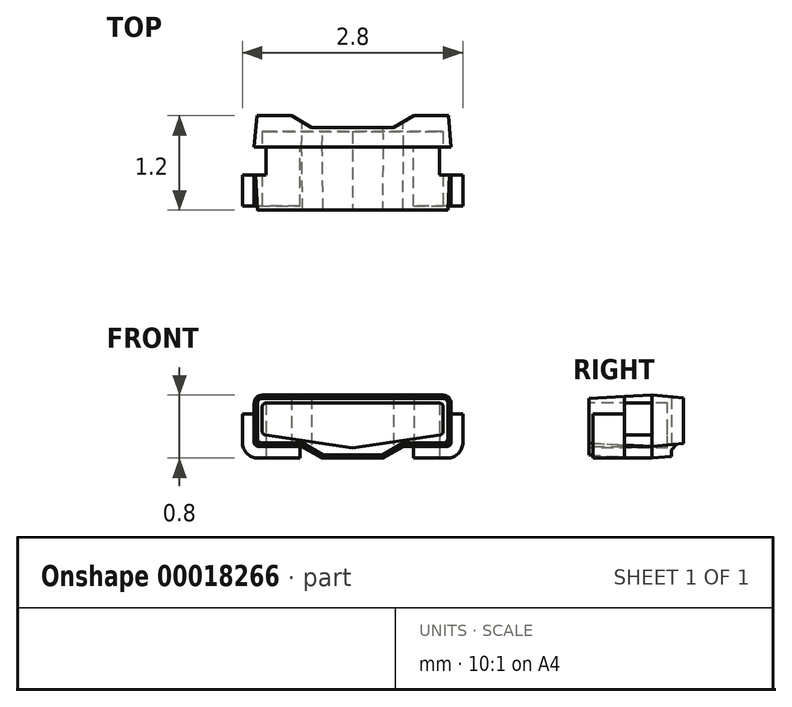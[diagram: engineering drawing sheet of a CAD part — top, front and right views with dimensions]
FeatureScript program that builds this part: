
annotation { "Feature Type Name" : "Feature", "Feature Type Description" : "" }
export const myFeature = defineFeature(function(context is Context, id is Id, definition is map)
    precondition{}
    {
        {
            var Q0;
            Q0=qCreatedBy(makeId("Front.planeOp"),FACE);
            var sketch = newSketch(context, id + "F0", { "sketchPlane" : qUnion([Q0])});
            skFitSpline(sketch, "E0", {"points": [v(1.14, 0.3) * mm, v(1.14, 0.3) * mm, v(1.15, 0.31) * mm, v(1.15, 0.32) * mm]});
            skLineSegment(sketch, "E1", {"start": v(0, 0.12) * mm, "end": v(1.14, 0.3) * mm});
            skLineSegment(sketch, "E2", {"start": v(-1.15, 0.76) * mm, "end": v(-1.15, 0.8) * mm});
            skLineSegment(sketch, "E3", {"start": v(-1.22, 0.7) * mm, "end": v(-1.25, 0.7) * mm});
            skLineSegment(sketch, "E4", {"start": v(-1.25, 0.25) * mm, "end": v(-1.22, 0.25) * mm});
            skLineSegment(sketch, "E5", {"start": v(-1.15, 0.15) * mm, "end": v(-1.15, 0.19) * mm});
            skLineSegment(sketch, "E6", {"start": v(-0.65, 0.15) * mm, "end": v(-0.64, 0.19) * mm});
            skLineSegment(sketch, "E7", {"start": v(-0.4, 0) * mm, "end": v(-0.38, 0.04) * mm});
            skLineSegment(sketch, "E8", {"start": v(0.38, 0.04) * mm, "end": v(0.39, 0) * mm});
            skLineSegment(sketch, "E9", {"start": v(0.65, 0.15) * mm, "end": v(0.63, 0.18) * mm});
            skLineSegment(sketch, "E10", {"start": v(1.15, 0.19) * mm, "end": v(1.15, 0.15) * mm});
            skLineSegment(sketch, "E11", {"start": v(1.21, 0.25) * mm, "end": v(1.25, 0.25) * mm});
            skLineSegment(sketch, "E12", {"start": v(1.21, 0.7) * mm, "end": v(1.25, 0.7) * mm});
            skLineSegment(sketch, "E13", {"start": v(1.15, 0.76) * mm, "end": v(1.15, 0.8) * mm});
            skLineSegment(sketch, "E14", {"start": v(0, 0.12) * mm, "end": v(-1.14, 0.3) * mm});
            skFitSpline(sketch, "E15", {"points": [v(-1.15, 0.32) * mm, v(-1.15, 0.31) * mm, v(-1.15, 0.3) * mm, v(-1.14, 0.3) * mm]});
            skLineSegment(sketch, "E16", {"start": v(1.15, 0.68) * mm, "end": v(1.15, 0.32) * mm});
            skLineSegment(sketch, "E17", {"start": v(-1.14, 0.3) * mm, "end": v(-1.14, 0.3) * mm});
            skLineSegment(sketch, "E18", {"start": v(-1.15, 0.32) * mm, "end": v(-1.15, 0.68) * mm});
            skLineSegment(sketch, "E19", {"start": v(-0.64, 0.19) * mm, "end": v(-0.38, 0.04) * mm});
            skLineSegment(sketch, "E20", {"start": v(-0.65, 0.15) * mm, "end": v(-0.4, 0) * mm});
            skLineSegment(sketch, "E21", {"start": v(0.63, 0.18) * mm, "end": v(0.38, 0.04) * mm});
            skLineSegment(sketch, "E22", {"start": v(0.65, 0.15) * mm, "end": v(0.39, 0) * mm});
            skLineSegment(sketch, "E23", {"start": v(0, 1.03) * mm, "end": v(0, -0.23) * mm});
            skLineSegment(sketch, "E24", {"start": v(-1.1, 0.15) * mm, "end": v(-1.1, 0) * mm});
            skFitSpline(sketch, "E25", {"points": [v(-1.4, 0.2) * mm, v(-1.4, 0.09) * mm, v(-1.31, 0) * mm, v(-1.2, 0) * mm]});
            skFitSpline(sketch, "E26", {"points": [v(-1.25, 0.2) * mm, v(-1.25, 0.17) * mm, v(-1.23, 0.15) * mm, v(-1.2, 0.15) * mm]});
            skLineSegment(sketch, "E27", {"start": v(-1.25, 0.4) * mm, "end": v(-1.25, 0.2) * mm});
            skLineSegment(sketch, "E28", {"start": v(-0.64, 0.19) * mm, "end": v(-1.15, 0.19) * mm});
            skFitSpline(sketch, "E29", {"points": [v(1.2, 0) * mm, v(1.3, 0) * mm, v(1.4, 0.09) * mm, v(1.4, 0.2) * mm]});
            skFitSpline(sketch, "E30", {"points": [v(1.2, 0.15) * mm, v(1.23, 0.15) * mm, v(1.25, 0.17) * mm, v(1.25, 0.2) * mm]});
            skLineSegment(sketch, "E31", {"start": v(-0.67, 0.15) * mm, "end": v(-1.2, 0.15) * mm});
            skLineSegment(sketch, "E32", {"start": v(1.1, 0.15) * mm, "end": v(1.1, 0) * mm});
            skLineSegment(sketch, "E33", {"start": v(1.21, 0.7) * mm, "end": v(1.21, 0.25) * mm});
            skLineSegment(sketch, "E34", {"start": v(1.25, 0.4) * mm, "end": v(1.25, 0.2) * mm});
            skLineSegment(sketch, "E35", {"start": v(0.63, 0.18) * mm, "end": v(1.15, 0.19) * mm});
            skLineSegment(sketch, "E36", {"start": v(0.77, 0.15) * mm, "end": v(1.2, 0.15) * mm});
            skLineSegment(sketch, "E37", {"start": v(-1.25, 0.56) * mm, "end": v(-1.4, 0.56) * mm});
            skFitSpline(sketch, "E38", {"points": [v(-1.14, 0.69) * mm, v(-1.15, 0.69) * mm, v(-1.15, 0.68) * mm, v(-1.15, 0.68) * mm]});
            skFitSpline(sketch, "E39", {"points": [v(1.15, 0.68) * mm, v(1.15, 0.68) * mm, v(1.14, 0.69) * mm, v(1.14, 0.69) * mm]});
            skLineSegment(sketch, "E40", {"start": v(1.4, 0.56) * mm, "end": v(1.25, 0.56) * mm});
            skLineSegment(sketch, "E41", {"start": v(1.14, 0.69) * mm, "end": v(-1.14, 0.69) * mm});
            skFitSpline(sketch, "E42", {"points": [v(-1.22, 0.25) * mm, v(-1.22, 0.21) * mm, v(-1.19, 0.19) * mm, v(-1.15, 0.19) * mm]});
            skFitSpline(sketch, "E43", {"points": [v(-1.25, 0.25) * mm, v(-1.25, 0.2) * mm, v(-1.2, 0.15) * mm, v(-1.15, 0.15) * mm]});
            skLineSegment(sketch, "E44", {"start": v(1.54, 0.4) * mm, "end": v(-1.55, 0.4) * mm});
            skLineSegment(sketch, "E45", {"start": v(0.38, 0.04) * mm, "end": v(-0.38, 0.04) * mm});
            skLineSegment(sketch, "E46", {"start": v(0.39, 0) * mm, "end": v(-0.4, 0) * mm});
            skLineSegment(sketch, "E47", {"start": v(-0.65, 0.15) * mm, "end": v(-1.15, 0.15) * mm});
            skLineSegment(sketch, "E48", {"start": v(1.15, 0.15) * mm, "end": v(0.65, 0.15) * mm});
            skLineSegment(sketch, "E49", {"start": v(-0.67, 0) * mm, "end": v(-1.2, 0) * mm});
            skFitSpline(sketch, "E50", {"points": [v(-1.15, 0.76) * mm, v(-1.19, 0.76) * mm, v(-1.22, 0.74) * mm, v(-1.22, 0.7) * mm]});
            skFitSpline(sketch, "E51", {"points": [v(-1.15, 0.8) * mm, v(-1.2, 0.8) * mm, v(-1.25, 0.76) * mm, v(-1.25, 0.7) * mm]});
            skLineSegment(sketch, "E52", {"start": v(1.2, 0) * mm, "end": v(0.77, 0) * mm});
            skLineSegment(sketch, "E53", {"start": v(1.15, 0.76) * mm, "end": v(-1.15, 0.76) * mm});
            skLineSegment(sketch, "E54", {"start": v(1.15, 0.8) * mm, "end": v(-1.15, 0.8) * mm});
            skLineSegment(sketch, "E55", {"start": v(-1.22, 0.7) * mm, "end": v(-1.22, 0.25) * mm});
            skLineSegment(sketch, "E56", {"start": v(-1.25, 0.7) * mm, "end": v(-1.25, 0.25) * mm});
            skLineSegment(sketch, "E57", {"start": v(-0.67, 0.15) * mm, "end": v(-0.67, 0) * mm});
            skFitSpline(sketch, "E58", {"points": [v(1.21, 0.7) * mm, v(1.21, 0.74) * mm, v(1.18, 0.76) * mm, v(1.15, 0.76) * mm]});
            skFitSpline(sketch, "E59", {"points": [v(1.25, 0.7) * mm, v(1.25, 0.76) * mm, v(1.2, 0.8) * mm, v(1.15, 0.8) * mm]});
            skFitSpline(sketch, "E60", {"points": [v(1.15, 0.19) * mm, v(1.18, 0.19) * mm, v(1.21, 0.21) * mm, v(1.21, 0.25) * mm]});
            skFitSpline(sketch, "E61", {"points": [v(1.15, 0.15) * mm, v(1.2, 0.15) * mm, v(1.25, 0.2) * mm, v(1.25, 0.25) * mm]});
            skLineSegment(sketch, "E62", {"start": v(-1.4, 0.56) * mm, "end": v(-1.4, 0.2) * mm});
            skLineSegment(sketch, "E63", {"start": v(1.25, 0.7) * mm, "end": v(1.25, 0.25) * mm});
            skLineSegment(sketch, "E64", {"start": v(0.77, 0.15) * mm, "end": v(0.77, 0) * mm});
            skLineSegment(sketch, "E65", {"start": v(1.4, 0.56) * mm, "end": v(1.4, 0.2) * mm});
            skSolve(sketch);
        }
        {
            var Q0;
            Q0=qCreatedBy(makeId("Front.planeOp"),FACE);
            var sketch = newSketch(context, id + "F1", { "sketchPlane" : qUnion([Q0])});
            skLineSegment(sketch, "E66.rect.bottom", {"start": v(1.15, 0.15) * mm, "end": v(0.65, 0.15) * mm});
            skLineSegment(sketch, "E66.rect.top", {"start": v(1.15, 0.8) * mm, "end": v(0, 0.8) * mm});
            skLineSegment(sketch, "E66.rect.left", {"start": v(1.25, 0.25) * mm, "end": v(1.25, 0.7) * mm});
            skLineSegment(sketch, "E67", {"start": v(0.65, 0.15) * mm, "end": v(0.39, 0) * mm});
            skLineSegment(sketch, "E68", {"start": v(0.39, 0) * mm, "end": v(0, 0) * mm});
            skLineSegment(sketch, "E69", {"start": v(0, 0.8) * mm, "end": v(0, 0) * mm, "construction": true});
            skLineSegment(sketch, "E70", {"start": v(0, 0.7) * mm, "end": v(1.1, 0.7) * mm});
            skLineSegment(sketch, "E71", {"start": v(1.15, 0.65) * mm, "end": v(1.15, 0.34) * mm});
            skLineSegment(sketch, "E72", {"start": v(1.1, 0.3) * mm, "end": v(0, 0.13) * mm});
            skPoint(sketch, "E73.visualSharp", {"position": v(1.25, 0.8) * mm});
            skArc(sketch, "E73.filletArc", {"start": v(1.25, 0.7) * mm, "mid": v(1.22, 0.77) * mm, "end": v(1.15, 0.8) * mm});
            skPoint(sketch, "E74.visualSharp", {"position": v(1.25, 0.15) * mm});
            skArc(sketch, "E74.filletArc", {"start": v(1.15, 0.15) * mm, "mid": v(1.22, 0.18) * mm, "end": v(1.25, 0.25) * mm});
            skArc(sketch, "E75.MirrorCS", {"start": v(-1.15, 0.15) * mm, "mid": v(-1.22, 0.18) * mm, "end": v(-1.25, 0.25) * mm});
            skLineSegment(sketch, "E76.MirrorCS", {"start": v(-1.15, 0.65) * mm, "end": v(-1.15, 0.34) * mm});
            skPoint(sketch, "E77.MirrorP", {"position": v(-1.25, 0.15) * mm});
            skLineSegment(sketch, "E78.MirrorCS", {"start": v(-1.1, 0.3) * mm, "end": v(0, 0.13) * mm});
            skPoint(sketch, "E79.MirrorP", {"position": v(-1.25, 0.8) * mm});
            skLineSegment(sketch, "E80.MirrorCS", {"start": v(-0.65, 0.15) * mm, "end": v(-0.39, 0) * mm});
            skLineSegment(sketch, "E81.MirrorCS", {"start": v(-1.25, 0.25) * mm, "end": v(-1.25, 0.7) * mm});
            skLineSegment(sketch, "E82.MirrorCS", {"start": v(0, 0.7) * mm, "end": v(-1.1, 0.7) * mm});
            skLineSegment(sketch, "E83.MirrorCS", {"start": v(-1.15, 0.8) * mm, "end": v(0, 0.8) * mm});
            skLineSegment(sketch, "E84.MirrorCS", {"start": v(-1.15, 0.15) * mm, "end": v(-0.65, 0.15) * mm});
            skLineSegment(sketch, "E85.MirrorCS", {"start": v(-0.39, 0) * mm, "end": v(0, 0) * mm});
            skArc(sketch, "E86.MirrorCS", {"start": v(-1.25, 0.7) * mm, "mid": v(-1.22, 0.77) * mm, "end": v(-1.15, 0.8) * mm});
            skArc(sketch, "E87.filletArc", {"start": v(1.15, 0.65) * mm, "mid": v(1.14, 0.69) * mm, "end": v(1.1, 0.7) * mm});
            skPoint(sketch, "E88.visualSharp", {"position": v(1.15, 0.3) * mm});
            skArc(sketch, "E88.filletArc", {"start": v(1.1, 0.3) * mm, "mid": v(1.14, 0.31) * mm, "end": v(1.15, 0.34) * mm});
            skArc(sketch, "E89.filletArc", {"start": v(-1.1, 0.7) * mm, "mid": v(-1.14, 0.69) * mm, "end": v(-1.15, 0.65) * mm});
            skPoint(sketch, "E90.visualSharp", {"position": v(-1.15, 0.3) * mm});
            skArc(sketch, "E90.filletArc", {"start": v(-1.15, 0.34) * mm, "mid": v(-1.14, 0.31) * mm, "end": v(-1.1, 0.3) * mm});
            skSolve(sketch);
        }
        {
            var Q0;
            Q0=qCreatedBy(makeId("Front.planeOp"),FACE);
            var sketch = newSketch(context, id + "F2", { "sketchPlane" : qUnion([Q0])});
            skLineSegment(sketch, "E91", {"start": v(1.25, 0.56) * mm, "end": v(1.25, 0.2) * mm});
            skLineSegment(sketch, "E92", {"start": v(1.2, 0.15) * mm, "end": v(0.77, 0.15) * mm});
            skLineSegment(sketch, "E93", {"start": v(0.77, 0.15) * mm, "end": v(0.77, 0) * mm});
            skLineSegment(sketch, "E94", {"start": v(0.77, 0) * mm, "end": v(1.2, 0) * mm});
            skLineSegment(sketch, "E95", {"start": v(1.4, 0.2) * mm, "end": v(1.4, 0.56) * mm});
            skLineSegment(sketch, "E96", {"start": v(1.4, 0.56) * mm, "end": v(1.25, 0.56) * mm});
            skPoint(sketch, "E97.visualSharp", {"position": v(1.4, 0) * mm});
            skArc(sketch, "E97.filletArc", {"start": v(1.2, 0) * mm, "mid": v(1.34, 0.06) * mm, "end": v(1.4, 0.2) * mm});
            skPoint(sketch, "E98.visualSharp", {"position": v(1.25, 0.15) * mm});
            skArc(sketch, "E98.filletArc", {"start": v(1.2, 0.15) * mm, "mid": v(1.24, 0.16) * mm, "end": v(1.25, 0.2) * mm});
            skLineSegment(sketch, "E99", {"start": v(0, 1.1) * mm, "end": v(0, -0.4) * mm, "construction": true});
            skArc(sketch, "E100.MirrorCS", {"start": v(-1.2, 0.15) * mm, "mid": v(-1.24, 0.16) * mm, "end": v(-1.25, 0.2) * mm});
            skLineSegment(sketch, "E101.MirrorCS", {"start": v(-1.4, 0.2) * mm, "end": v(-1.4, 0.56) * mm});
            skLineSegment(sketch, "E102.MirrorCS", {"start": v(-1.4, 0.56) * mm, "end": v(-1.25, 0.56) * mm});
            skPoint(sketch, "E103.MirrorP", {"position": v(-1.25, 0.15) * mm});
            skLineSegment(sketch, "E104.MirrorCS", {"start": v(-1.25, 0.56) * mm, "end": v(-1.25, 0.2) * mm});
            skArc(sketch, "E105.MirrorCS", {"start": v(-1.2, 0) * mm, "mid": v(-1.34, 0.06) * mm, "end": v(-1.4, 0.2) * mm});
            skPoint(sketch, "E106.MirrorP", {"position": v(-1.4, 0) * mm});
            skLineSegment(sketch, "E107", {"start": v(-1.2, 0.15) * mm, "end": v(-0.67, 0.15) * mm});
            skLineSegment(sketch, "E108", {"start": v(-0.67, 0.15) * mm, "end": v(-0.67, 0) * mm});
            skLineSegment(sketch, "E109", {"start": v(-0.67, 0) * mm, "end": v(-1.2, 0) * mm});
            skSolve(sketch);
        }
        {
            var Q0;
            Q0 = qSketchRegion(id + "F1", true);
            var Q1;
            Q1=makeQuery(id+"F1.imprint","IMPRINT",FACE,{"disambiguationData":[TD([[makeQuery(id+"F1.imprint","IMPRINT",EDGE,{"derivedFrom":sQuery(id+"F1.wireOp",EDGE,"E70")}),-1.0]])]});
            extrude(context, id + "F3", {"entities" : qUnion([Q0, Q1]), "depth" : 0.8 * mm, "hasDraft" : true, "draftAngle" : 3 * degree, "draftPullDirection" : true, "hasSecondDirection" : true, "secondDirectionOppositeDirection" : true, "secondDirectionDepth" : 0.4 * mm, "hasSecondDirectionDraft" : true, "secondDirectionDraftAngle" : 5 * degree, "secondDirectionDraftPullDirection" : true});
        }
        {
            var Q0;
            Q0=makeQuery(id+"F3.opExtrude","CAP_FACE",FACE,{"disambiguationData":[OSD([sQuery(id+"F1.wireOp",EDGE,"E66.rect.bottom"),sQuery(id+"F1.wireOp",EDGE,"E66.rect.top"),sQuery(id+"F1.wireOp",EDGE,"E66.rect.left"),sQuery(id+"F1.wireOp",EDGE,"E67"),sQuery(id+"F1.wireOp",EDGE,"E68"),sQuery(id+"F1.wireOp",EDGE,"E73.filletArc"),sQuery(id+"F1.wireOp",EDGE,"E74.filletArc"),sQuery(id+"F1.wireOp",EDGE,"E75.MirrorCS"),sQuery(id+"F1.wireOp",EDGE,"E80.MirrorCS"),sQuery(id+"F1.wireOp",EDGE,"E81.MirrorCS"),sQuery(id+"F1.wireOp",EDGE,"E83.MirrorCS"),sQuery(id+"F1.wireOp",EDGE,"E84.MirrorCS"),sQuery(id+"F1.wireOp",EDGE,"E85.MirrorCS"),sQuery(id+"F1.wireOp",EDGE,"E86.MirrorCS")])],"isStart":false});
            var sketch = newSketch(context, id + "F4", { "sketchPlane" : qUnion([Q0])});
            skLineSegment(sketch, "E110.0.0", {"start": v(1.1, 0.7) * mm, "end": v(0, 0.7) * mm});
            skLineSegment(sketch, "E110.0.1", {"start": v(0, 0.7) * mm, "end": v(-1.1, 0.7) * mm});
            skArc(sketch, "E110.0.2", {"start": v(-1.1, 0.7) * mm, "mid": v(-1.14, 0.69) * mm, "end": v(-1.15, 0.65) * mm});
            skLineSegment(sketch, "E110.0.3", {"start": v(-1.15, 0.65) * mm, "end": v(-1.15, 0.34) * mm});
            skArc(sketch, "E110.0.4", {"start": v(-1.15, 0.34) * mm, "mid": v(-1.14, 0.31) * mm, "end": v(-1.1, 0.3) * mm});
            skLineSegment(sketch, "E110.0.5", {"start": v(-1.1, 0.3) * mm, "end": v(0, 0.13) * mm});
            skLineSegment(sketch, "E110.0.6", {"start": v(0, 0.13) * mm, "end": v(1.1, 0.3) * mm});
            skArc(sketch, "E110.0.7", {"start": v(1.1, 0.3) * mm, "mid": v(1.14, 0.31) * mm, "end": v(1.15, 0.34) * mm});
            skLineSegment(sketch, "E110.0.8", {"start": v(1.15, 0.34) * mm, "end": v(1.15, 0.65) * mm});
            skArc(sketch, "E110.0.9", {"start": v(1.15, 0.65) * mm, "mid": v(1.14, 0.69) * mm, "end": v(1.1, 0.7) * mm});
            skSolve(sketch);
        }
        {
            var Q0;
            Q0 = qSketchRegion(id + "F4", true);
            extrude(context, id + "F5", {"entities" : qUnion([Q0]), "operationType" : NewBodyOperationType.REMOVE, "oppositeDirection" : true, "depth" : 1 * mm});
        }
        {
            var Q0;
            Q0 = qSketchRegion(id + "F4", true);
            extrude(context, id + "F6", {"entities" : qUnion([Q0]), "oppositeDirection" : true, "depth" : 1 * mm});
        }
        {
            var Q0;
            Q0 = qSketchRegion(id + "F2", true);
            extrude(context, id + "F7", {"entities" : qUnion([Q0]), "operationType" : NewBodyOperationType.ADD, "depth" : 0.75 * mm});
        }
        {
            var Q0;
            Q0=qCreatedBy(makeId("Top.planeOp"),FACE);
            var sketch = newSketch(context, id + "F8", { "sketchPlane" : qUnion([Q0])});
            skLineSegment(sketch, "E111.bottom", {"start": v(-1.4, 0) * mm, "end": v(-1.1, 0) * mm});
            skLineSegment(sketch, "E111.top", {"start": v(-1.4, -0.35) * mm, "end": v(-1.1, -0.35) * mm});
            skLineSegment(sketch, "E111.left", {"start": v(-1.4, 0) * mm, "end": v(-1.4, -0.35) * mm});
            skLineSegment(sketch, "E111.right", {"start": v(-1.1, 0) * mm, "end": v(-1.1, -0.35) * mm});
            skLineSegment(sketch, "E112", {"start": v(0, -1.25) * mm, "end": v(0, 1.01) * mm, "construction": true});
            skLineSegment(sketch, "E113.MirrorCS", {"start": v(1.4, 0) * mm, "end": v(1.4, -0.35) * mm});
            skLineSegment(sketch, "E114.MirrorCS", {"start": v(1.4, -0.35) * mm, "end": v(1.1, -0.35) * mm});
            skLineSegment(sketch, "E115.MirrorCS", {"start": v(1.1, 0) * mm, "end": v(1.1, -0.35) * mm});
            skLineSegment(sketch, "E116.MirrorCS", {"start": v(1.4, 0) * mm, "end": v(1.1, 0) * mm});
            skSolve(sketch);
        }
        {
            var Q0;
            Q0 = qSketchRegion(id + "F8", true);
            extrude(context, id + "F9", {"entities" : qUnion([Q0]), "operationType" : NewBodyOperationType.REMOVE, "endBound" : BoundingType.THROUGH_ALL, "depth" : 25 * mm});
        }
        {
            var Q0;
            Q0=qCreatedBy(makeId("Top.planeOp"),FACE);
            var sketch = newSketch(context, id + "F10", { "sketchPlane" : qUnion([Q0])});
            skLineSegment(sketch, "E117", {"start": v(-0.78, 0.4) * mm, "end": v(-0.52, 0.25) * mm});
            skLineSegment(sketch, "E118", {"start": v(-0.52, 0.25) * mm, "end": v(0, 0.25) * mm});
            skLineSegment(sketch, "E119", {"start": v(-0.78, 0.4) * mm, "end": v(0, 0.4) * mm});
            skLineSegment(sketch, "E120", {"start": v(0, 0) * mm, "end": v(0, 0.4) * mm, "construction": true});
            skLineSegment(sketch, "E121.MirrorCS", {"start": v(0.78, 0.4) * mm, "end": v(0, 0.4) * mm});
            skLineSegment(sketch, "E122.MirrorCS", {"start": v(0.78, 0.4) * mm, "end": v(0.52, 0.25) * mm});
            skLineSegment(sketch, "E123.MirrorCS", {"start": v(0.52, 0.25) * mm, "end": v(0, 0.25) * mm});
            skSolve(sketch);
        }
        {
            var Q0;
            Q0 = qSketchRegion(id + "F10", true);
            extrude(context, id + "F11", {"entities" : qUnion([Q0]), "operationType" : NewBodyOperationType.REMOVE, "endBound" : BoundingType.THROUGH_ALL, "depth" : 25 * mm});
        }
    });
